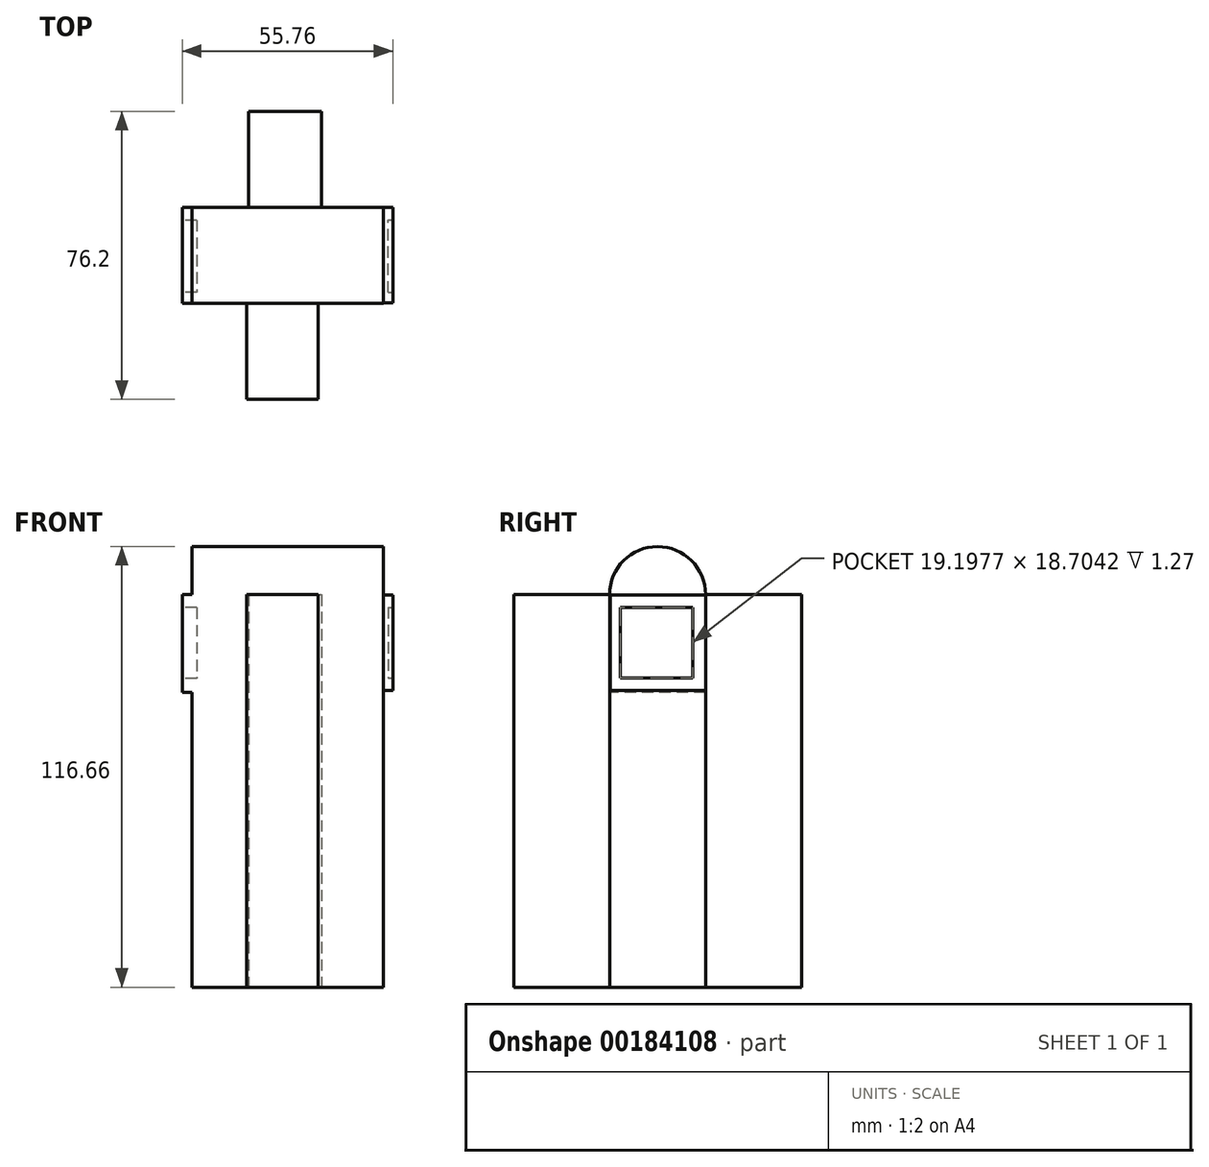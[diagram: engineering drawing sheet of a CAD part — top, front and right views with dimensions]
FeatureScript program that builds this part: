
annotation { "Feature Type Name" : "Feature", "Feature Type Description" : "" }
export const myFeature = defineFeature(function(context is Context, id is Id, definition is map)
    precondition{}
    {
        {
            var Q0;
            Q0=qCreatedBy(makeId("Front.planeOp"),FACE);
            var sketch = newSketch(context, id + "F0", { "sketchPlane" : qUnion([Q0])});
            skLineSegment(sketch, "E0.bottom", {"start": v(-23.52, 51.72) * mm, "end": v(27.16, 51.72) * mm});
            skLineSegment(sketch, "E0.top", {"start": v(-23.52, -52.24) * mm, "end": v(27.16, -52.24) * mm});
            skLineSegment(sketch, "E0.left", {"start": v(-23.52, 51.72) * mm, "end": v(-23.52, -52.24) * mm});
            skLineSegment(sketch, "E0.right", {"start": v(27.16, 51.72) * mm, "end": v(27.16, -52.24) * mm});
            skSolve(sketch);
        }
        {
            var Q0;
            Q0=makeQuery(id+"F0.imprint","IMPRINT",FACE,{"disambiguationData":[TD([[makeQuery(id+"F0.imprint","IMPRINT",EDGE,{"derivedFrom":sQuery(id+"F0.wireOp",EDGE,"E0.bottom")}),-1.0]])]});
            extrude(context, id + "F1", {"entities" : qUnion([Q0]), "depth" : 25.4 * mm});
        }
        {
            var Q0;
            Q0=makeQuery(id+"F1.opExtrude","SWEPT_FACE",FACE,{"disambiguationData":[OSD([sQuery(id+"F0.wireOp",EDGE,"E0.right")])]});
            var sketch = newSketch(context, id + "F2", { "sketchPlane" : qUnion([Q0])});
            skArc(sketch, "E1", {"start": v(0, 51.72) * mm, "mid": v(-12.7, 64.42) * mm, "end": v(-25.4, 51.72) * mm});
            skSolve(sketch);
        }
        {
            var Q0;
            Q0=makeQuery(id+"F1.opExtrude","SWEPT_FACE",FACE,{"disambiguationData":[OSD([sQuery(id+"F0.wireOp",EDGE,"E0.left")])]});
            var sketch = newSketch(context, id + "F3", { "sketchPlane" : qUnion([Q0])});
            skArc(sketch, "E2", {"start": v(25.4, 51.72) * mm, "mid": v(12.7, 64.42) * mm, "end": v(0, 51.72) * mm});
            skSolve(sketch);
        }
        {
            var Q0;
            Q0=makeQuery(id+"F1.opExtrude","CAP_FACE",FACE,{"disambiguationData":[OSD([sQuery(id+"F0.wireOp",EDGE,"E0.bottom"),sQuery(id+"F0.wireOp",EDGE,"E0.top"),sQuery(id+"F0.wireOp",EDGE,"E0.left"),sQuery(id+"F0.wireOp",EDGE,"E0.right")])],"isStart":false});
            var sketch = newSketch(context, id + "F4", { "sketchPlane" : qUnion([Q0])});
            skLineSegment(sketch, "E3", {"start": v(-8.94, 51.72) * mm, "end": v(-8.94, -52.24) * mm});
            skLineSegment(sketch, "E4", {"start": v(9.98, 51.72) * mm, "end": v(9.98, -52.24) * mm});
            skSolve(sketch);
        }
        {
            var Q0;
            {var subQ0=sQuery(id+"F4.wireOp",EDGE,"E3");Q0=makeQuery(id+"F4.imprint","IMPRINT",FACE,{"disambiguationData":[TD([[makeQuery(id+"F4.imprint","IMPRINT",EDGE,{"derivedFrom":subQ0}),1.0]])]});}
            extrude(context, id + "F5", {"entities" : qUnion([Q0]), "operationType" : NewBodyOperationType.ADD, "depth" : 25.4 * mm});
        }
        {
            var Q0;
            Q0=makeQuery(id+"F1.opExtrude","CAP_FACE",FACE,{"disambiguationData":[OSD([sQuery(id+"F0.wireOp",EDGE,"E0.bottom"),sQuery(id+"F0.wireOp",EDGE,"E0.top"),sQuery(id+"F0.wireOp",EDGE,"E0.left"),sQuery(id+"F0.wireOp",EDGE,"E0.right")])],"isStart":true});
            var sketch = newSketch(context, id + "F6", { "sketchPlane" : qUnion([Q0])});
            skLineSegment(sketch, "E5", {"start": v(8.5, 51.72) * mm, "end": v(8.5, -52.24) * mm});
            skLineSegment(sketch, "E6", {"start": v(-10.77, 51.72) * mm, "end": v(-10.77, -52.24) * mm});
            skPoint(sketch, "E7.end.orphan", {"position": v(8.5, -52.24) * mm});
            skSolve(sketch);
        }
        {
            var Q0;
            {var subQ0=sQuery(id+"F6.wireOp",EDGE,"E5");Q0=makeQuery(id+"F6.imprint","IMPRINT",FACE,{"disambiguationData":[TD([[makeQuery(id+"F6.imprint","IMPRINT",EDGE,{"derivedFrom":subQ0}),-1.0]])]});}
            extrude(context, id + "F7", {"entities" : qUnion([Q0]), "operationType" : NewBodyOperationType.ADD, "depth" : 25.4 * mm});
        }
        {
            var Q0;
            {var subQ0=sQuery(id+"F0.wireOp",EDGE,"E0.bottom");Q0=makeQuery(id+"F7.boolean.opBoolean","MERGE",FACE,{"derivedFrom":[makeQuery(id+"F5.boolean.opBoolean","MERGE",FACE,{"derivedFrom":[makeQuery(id+"F1.opExtrude","SWEPT_FACE",FACE,{"disambiguationData":[OSD([subQ0])]}),makeQuery(id+"F5.opExtrude","SWEPT_FACE",FACE,{"disambiguationData":[OSD([subQ0])]})]}),makeQuery(id+"F7.opExtrude","SWEPT_FACE",FACE,{"disambiguationData":[OSD([subQ0])]})]});}
            var sketch = newSketch(context, id + "F8", { "sketchPlane" : qUnion([Q0])});
            skLineSegment(sketch, "E8", {"start": v(-23.52, -12.7) * mm, "end": v(27.16, -12.7) * mm});
            skSolve(sketch);
        }
        {
            var Q0;
            Q0=makeQuery(id+"F3.imprint","IMPRINT",FACE,{"disambiguationData":[TD([[makeQuery(id+"F3.imprint","IMPRINT",EDGE,{"derivedFrom":sQuery(id+"F3.wireOp",EDGE,"E2")}),1.0]])]});
            var Q1;
            Q1=sQuery(id+"F8.wireOp",EDGE,"E8");
            sweep(context, id + "F9", {"operationType" : NewBodyOperationType.ADD, "profiles" : qUnion([Q0]), "path" : qUnion([Q1])});
        }
        {
            var Q0;
            {var subQ0=sQuery(id+"F0.wireOp",EDGE,"E0.right");Q0=makeQuery(id+"F2.imprint","IMPRINT",FACE,{"disambiguationData":[TD([[makeQuery(id+"F2.imprint","IMPRINT",EDGE,{"derivedFrom":makeQuery(id+"F1.opExtrude","CAP_EDGE",EDGE,{"disambiguationData":[OSD([subQ0])],"isStart":true})}),-1.0]])]});}
            var sketch = newSketch(context, id + "F10", { "sketchPlane" : qUnion([Q0])});
            skPoint(sketch, "E9", {"position": v(-25.25, 0) * mm});
            skPoint(sketch, "E10", {"position": v(-25.25, 26.38) * mm});
            skPoint(sketch, "E11", {"position": v(0, 26.38) * mm});
            skPoint(sketch, "E12", {"position": v(-25.25, 51.55) * mm});
            skPoint(sketch, "E13", {"position": v(0, 51.55) * mm});
            skLineSegment(sketch, "E14.bottom", {"start": v(-25.25, 51.55) * mm, "end": v(0, 51.55) * mm});
            skLineSegment(sketch, "E14.top", {"start": v(-25.25, 26.38) * mm, "end": v(0, 26.38) * mm});
            skLineSegment(sketch, "E14.left", {"start": v(-25.25, 51.55) * mm, "end": v(-25.25, 26.38) * mm});
            skLineSegment(sketch, "E14.right", {"start": v(0, 51.55) * mm, "end": v(0, 26.38) * mm});
            skSolve(sketch);
        }
        {
            var Q0;
            Q0=makeQuery(id+"F10.imprint","IMPRINT",FACE,{"disambiguationData":[TD([[makeQuery(id+"F10.imprint","IMPRINT",EDGE,{"derivedFrom":sQuery(id+"F10.wireOp",EDGE,"E14.bottom")}),-1.0]])]});
            extrude(context, id + "F11", {"entities" : qUnion([Q0]), "operationType" : NewBodyOperationType.ADD, "depth" : 2.54 * mm});
        }
        {
            var Q0;
            {var subQ0=sQuery(id+"F0.wireOp",EDGE,"E0.right");Q0=makeQuery(id+"F2.imprint","IMPRINT",FACE,{"disambiguationData":[TD([[makeQuery(id+"F2.imprint","IMPRINT",EDGE,{"derivedFrom":makeQuery(id+"F1.opExtrude","CAP_EDGE",EDGE,{"disambiguationData":[OSD([subQ0])],"isStart":true})}),-1.0]])]});}
            var sketch = newSketch(context, id + "F12", { "sketchPlane" : qUnion([Q0])});
            skLineSegment(sketch, "E15", {"start": v(-25.25, 26.2) * mm, "end": v(-25.25, -52.07) * mm});
            skLineSegment(sketch, "E16", {"start": v(-25.25, -52.07) * mm, "end": v(0, 25.69) * mm});
            skSolve(sketch);
        }
        {
            var Q0;
            {var subQ0=sQuery(id+"F0.wireOp",EDGE,"E0.right");Q0=makeQuery(id+"F2.imprint","IMPRINT",FACE,{"disambiguationData":[TD([[makeQuery(id+"F2.imprint","IMPRINT",EDGE,{"derivedFrom":makeQuery(id+"F1.opExtrude","CAP_EDGE",EDGE,{"disambiguationData":[OSD([subQ0])],"isStart":true})}),-1.0]])]});}
            var sketch = newSketch(context, id + "F13", { "sketchPlane" : qUnion([Q0])});
            skLineSegment(sketch, "E17", {"start": v(-23.7, 26.2) * mm, "end": v(-23.7, -45.82) * mm});
            skLineSegment(sketch, "E18", {"start": v(-23.7, -45.82) * mm, "end": v(-23.7, 26.2) * mm});
            skLineSegment(sketch, "E19", {"start": v(-20.4, 25.86) * mm, "end": v(-20.4, -36.27) * mm});
            skLineSegment(sketch, "E20", {"start": v(-16.57, 25.86) * mm, "end": v(-16.57, -24.65) * mm});
            skLineSegment(sketch, "E21", {"start": v(-12.93, 25.86) * mm, "end": v(-12.93, -13.02) * mm});
            skLineSegment(sketch, "E22", {"start": v(-9.29, 25.86) * mm, "end": v(-9.29, -1.9) * mm});
            skLineSegment(sketch, "E23", {"start": v(-5.81, 25.69) * mm, "end": v(-5.81, 8.5) * mm});
            skLineSegment(sketch, "E24", {"start": v(-2.52, 25.86) * mm, "end": v(-2.52, 18.57) * mm});
            skLineSegment(sketch, "E25", {"start": v(-2.52, 18.57) * mm, "end": v(-23.7, 18.57) * mm});
            skLineSegment(sketch, "E26", {"start": v(-23.7, 18.57) * mm, "end": v(-5.81, 8.5) * mm});
            skLineSegment(sketch, "E27", {"start": v(-5.81, 8.5) * mm, "end": v(-23.7, 8.5) * mm});
            skLineSegment(sketch, "E28", {"start": v(-23.7, 8.5) * mm, "end": v(-9.29, -1.9) * mm});
            skLineSegment(sketch, "E29", {"start": v(-9.29, -1.9) * mm, "end": v(-23.7, -1.9) * mm});
            skLineSegment(sketch, "E30", {"start": v(-23.7, -1.9) * mm, "end": v(-12.93, -13.02) * mm});
            skLineSegment(sketch, "E31", {"start": v(-12.93, -13.02) * mm, "end": v(-23.7, -13.02) * mm});
            skLineSegment(sketch, "E32", {"start": v(-23.7, -13.02) * mm, "end": v(-16.57, -24.65) * mm});
            skLineSegment(sketch, "E33", {"start": v(-16.57, -24.65) * mm, "end": v(-23.7, -24.65) * mm});
            skLineSegment(sketch, "E34", {"start": v(-23.7, -24.65) * mm, "end": v(-20.4, -36.27) * mm});
            skLineSegment(sketch, "E35", {"start": v(-23.7, -36.27) * mm, "end": v(-22.05, -41.3) * mm});
            skLineSegment(sketch, "E36", {"start": v(-22.05, -41.3) * mm, "end": v(-23.7, -41.3) * mm});
            skLineSegment(sketch, "E37", {"start": v(-23.7, -41.3) * mm, "end": v(-23.7, -45.82) * mm});
            skSolve(sketch);
        }
        {
            var Q0;
            {var subQ0=sQuery(id+"F0.wireOp",EDGE,"E0.right");Q0=makeQuery(id+"F2.imprint","IMPRINT",FACE,{"disambiguationData":[TD([[makeQuery(id+"F2.imprint","IMPRINT",EDGE,{"derivedFrom":makeQuery(id+"F1.opExtrude","CAP_EDGE",EDGE,{"disambiguationData":[OSD([subQ0])],"isStart":true})}),-1.0]])]});}
            var sketch = newSketch(context, id + "F14", { "sketchPlane" : qUnion([Q0])});
            skSolve(sketch);
        }
        {
            var Q0;
            Q0=sQuery(id+"F13.wireOp",EDGE,"E25");
            extrude(context, id + "F15", {"bodyType" : ToolBodyType.SURFACE, "surfaceEntities" : qUnion([Q0]), "depth" : 1.27 * mm});
        }
        {
            var Q0;
            Q0=sQuery(id+"F13.wireOp",EDGE,"E18");
            extrude(context, id + "F16", {"bodyType" : ToolBodyType.SURFACE, "operationType" : NewBodyOperationType.ADD, "surfaceEntities" : qUnion([Q0]), "depth" : 1.27 * mm});
        }
        {
            var Q0;
            Q0=sQuery(id+"F13.wireOp",EDGE,"E19");
            extrude(context, id + "F17", {"bodyType" : ToolBodyType.SURFACE, "surfaceEntities" : qUnion([Q0]), "depth" : 1.27 * mm});
        }
        {
            var Q0;
            Q0=sQuery(id+"F13.wireOp",EDGE,"E20");
            extrude(context, id + "F18", {"bodyType" : ToolBodyType.SURFACE, "surfaceEntities" : qUnion([Q0]), "depth" : 1.27 * mm});
        }
        {
            var Q0;
            Q0=sQuery(id+"F13.wireOp",EDGE,"E21");
            var Q1;
            Q1=sQuery(id+"F13.wireOp",EDGE,"E22");
            extrude(context, id + "F19", {"bodyType" : ToolBodyType.SURFACE, "surfaceEntities" : qUnion([Q0, Q1]), "depth" : 1.27 * mm});
        }
        {
            var Q0;
            Q0=sQuery(id+"F13.wireOp",EDGE,"E23");
            var Q1;
            Q1=sQuery(id+"F13.wireOp",EDGE,"E24");
            extrude(context, id + "F20", {"bodyType" : ToolBodyType.SURFACE, "surfaceEntities" : qUnion([Q0, Q1]), "depth" : 1.27 * mm});
        }
        {
            var Q0;
            Q0=sQuery(id+"F13.wireOp",EDGE,"E26");
            extrude(context, id + "F21", {"bodyType" : ToolBodyType.SURFACE, "surfaceEntities" : qUnion([Q0]), "depth" : 1.27 * mm});
        }
        {
            var Q0;
            Q0=sQuery(id+"F13.wireOp",EDGE,"E27");
            extrude(context, id + "F22", {"bodyType" : ToolBodyType.SURFACE, "surfaceEntities" : qUnion([Q0]), "depth" : 1.27 * mm});
        }
        {
            var Q0;
            Q0=sQuery(id+"F13.wireOp",EDGE,"E28");
            extrude(context, id + "F23", {"bodyType" : ToolBodyType.SURFACE, "surfaceEntities" : qUnion([Q0]), "depth" : 1.27 * mm});
        }
        {
            var Q0;
            Q0=sQuery(id+"F13.wireOp",EDGE,"E29");
            extrude(context, id + "F24", {"bodyType" : ToolBodyType.SURFACE, "surfaceEntities" : qUnion([Q0]), "depth" : 1.27 * mm});
        }
        {
            var Q0;
            Q0=sQuery(id+"F13.wireOp",EDGE,"E30");
            var Q1;
            Q1=sQuery(id+"F13.wireOp",EDGE,"E31");
            extrude(context, id + "F25", {"bodyType" : ToolBodyType.SURFACE, "surfaceEntities" : qUnion([Q0, Q1]), "depth" : 1.27 * mm});
        }
        {
            var Q0;
            Q0=sQuery(id+"F13.wireOp",EDGE,"E32");
            var Q1;
            Q1=sQuery(id+"F13.wireOp",EDGE,"E33");
            extrude(context, id + "F26", {"bodyType" : ToolBodyType.SURFACE, "surfaceEntities" : qUnion([Q0, Q1]), "depth" : 1.27 * mm});
        }
        {
            var Q0;
            Q0=sQuery(id+"F13.wireOp",EDGE,"E34");
            var Q1;
            Q1=sQuery(id+"F13.wireOp",EDGE,"E35");
            extrude(context, id + "F27", {"bodyType" : ToolBodyType.SURFACE, "surfaceEntities" : qUnion([Q0, Q1]), "depth" : 1.27 * mm});
        }
        {
            var Q0;
            Q0=makeQuery(id+"F11.opExtrude","CAP_FACE",FACE,{"disambiguationData":[OSD([sQuery(id+"F10.wireOp",EDGE,"E14.bottom"),sQuery(id+"F10.wireOp",EDGE,"E14.top"),sQuery(id+"F10.wireOp",EDGE,"E14.left"),sQuery(id+"F10.wireOp",EDGE,"E14.right")])],"isStart":false});
            var sketch = newSketch(context, id + "F28", { "sketchPlane" : qUnion([Q0])});
            skLineSegment(sketch, "E38.bottom", {"start": v(-22.53, 48.32) * mm, "end": v(-3.33, 48.32) * mm});
            skLineSegment(sketch, "E38.top", {"start": v(-22.53, 29.62) * mm, "end": v(-3.33, 29.62) * mm});
            skLineSegment(sketch, "E38.left", {"start": v(-22.53, 48.32) * mm, "end": v(-22.53, 29.62) * mm});
            skLineSegment(sketch, "E38.right", {"start": v(-3.33, 48.32) * mm, "end": v(-3.33, 29.62) * mm});
            skSolve(sketch);
        }
        {
            var Q0;
            Q0=makeQuery(id+"F28.imprint","IMPRINT",FACE,{"disambiguationData":[TD([[makeQuery(id+"F28.imprint","IMPRINT",EDGE,{"derivedFrom":sQuery(id+"F28.wireOp",EDGE,"E38.bottom")}),-1.0]])]});
            extrude(context, id + "F29", {"entities" : qUnion([Q0]), "operationType" : NewBodyOperationType.REMOVE, "oppositeDirection" : true, "depth" : 1.27 * mm});
        }
        {
            var Q0;
            {var subQ0=sQuery(id+"F0.wireOp",EDGE,"E0.left");Q0=makeQuery(id+"F9.boolean.opBoolean","MERGE",FACE,{"derivedFrom":[makeQuery(id+"F1.opExtrude","SWEPT_FACE",FACE,{"disambiguationData":[OSD([subQ0])]}),makeQuery(id+"F9.opSweep","CAP_FACE",FACE,{"disambiguationData":[OSD([sQuery(id+"F0.wireOp",EDGE,"E0.bottom"),subQ0,sQuery(id+"F3.wireOp",EDGE,"E2"),sQuery(id+"F8.wireOp",VERTEX,"E8.start")])],"isStart":true})]});}
            var sketch = newSketch(context, id + "F30", { "sketchPlane" : qUnion([Q0])});
            skLineSegment(sketch, "E39.bottom", {"start": v(3.38, 48.25) * mm, "end": v(22.48, 48.25) * mm});
            skLineSegment(sketch, "E39.top", {"start": v(3.38, 29.5) * mm, "end": v(22.48, 29.5) * mm});
            skLineSegment(sketch, "E39.left", {"start": v(3.38, 48.25) * mm, "end": v(3.38, 29.5) * mm});
            skLineSegment(sketch, "E39.right", {"start": v(22.48, 48.25) * mm, "end": v(22.48, 29.5) * mm});
            skSolve(sketch);
        }
        {
            var Q0;
            Q0=makeQuery(id+"F30.imprint","IMPRINT",FACE,{"disambiguationData":[TD([[makeQuery(id+"F30.imprint","IMPRINT",EDGE,{"derivedFrom":sQuery(id+"F30.wireOp",EDGE,"E39.bottom")}),-1.0]])]});
            extrude(context, id + "F31", {"entities" : qUnion([Q0]), "operationType" : NewBodyOperationType.REMOVE, "oppositeDirection" : true, "depth" : 1.27 * mm});
        }
        {
            var Q0;
            {var subQ0=sQuery(id+"F0.wireOp",EDGE,"E0.left");Q0=makeQuery(id+"F9.boolean.opBoolean","MERGE",FACE,{"derivedFrom":[makeQuery(id+"F1.opExtrude","SWEPT_FACE",FACE,{"disambiguationData":[OSD([subQ0])]}),makeQuery(id+"F9.opSweep","CAP_FACE",FACE,{"disambiguationData":[OSD([sQuery(id+"F0.wireOp",EDGE,"E0.bottom"),subQ0,sQuery(id+"F3.wireOp",EDGE,"E2"),sQuery(id+"F8.wireOp",VERTEX,"E8.start")])],"isStart":true})]});}
            var sketch = newSketch(context, id + "F32", { "sketchPlane" : qUnion([Q0])});
            skLineSegment(sketch, "E40.bottom", {"start": v(0, 51.72) * mm, "end": v(25.4, 51.72) * mm});
            skLineSegment(sketch, "E40.top", {"start": v(0, 25.86) * mm, "end": v(25.4, 25.86) * mm});
            skLineSegment(sketch, "E40.left", {"start": v(0, 51.72) * mm, "end": v(0, 25.86) * mm});
            skLineSegment(sketch, "E40.right", {"start": v(25.4, 51.72) * mm, "end": v(25.4, 25.86) * mm});
            skSolve(sketch);
        }
        {
            var Q0;
            Q0=makeQuery(id+"F32.imprint","IMPRINT",FACE,{"disambiguationData":[TD([[makeQuery(id+"F32.imprint","IMPRINT",EDGE,{"derivedFrom":sQuery(id+"F32.wireOp",EDGE,"E40.bottom")}),-1.0]])]});
            extrude(context, id + "F33", {"entities" : qUnion([Q0]), "operationType" : NewBodyOperationType.ADD, "depth" : 2.54 * mm});
        }
        {
            var Q0;
            {var subQ0=sQuery(id+"F0.wireOp",EDGE,"E0.top");var subQ2=sQuery(id+"F0.wireOp",EDGE,"E0.left");var subQ3=sQuery(id+"F0.wireOp",EDGE,"E0.bottom");Q0=makeQuery(id+"F33.boolean.opBoolean","SPLIT",FACE,{"disambiguationData":[TD([makeQuery(id+"F1.opExtrude","SWEPT_FACE",FACE,{"disambiguationData":[OSD([subQ0])]})])],"derivedFrom":makeQuery(id+"F9.boolean.opBoolean","MERGE",FACE,{"derivedFrom":[makeQuery(id+"F1.opExtrude","SWEPT_FACE",FACE,{"disambiguationData":[OSD([subQ2])]}),makeQuery(id+"F9.opSweep","CAP_FACE",FACE,{"disambiguationData":[OSD([subQ3,subQ2,sQuery(id+"F3.wireOp",EDGE,"E2"),sQuery(id+"F8.wireOp",VERTEX,"E8.start")])],"isStart":true})]})});}
            var sketch = newSketch(context, id + "F34", { "sketchPlane" : qUnion([Q0])});
            skLineSegment(sketch, "E41", {"start": v(25.4, 25.86) * mm, "end": v(0, -52.24) * mm});
            skSolve(sketch);
        }
        {
            var Q0;
            Q0=makeQuery(id+"F34.imprint","IMPRINT",FACE,{"disambiguationData":[TD([[makeQuery(id+"F34.imprint","IMPRINT",EDGE,{"derivedFrom":sQuery(id+"F34.wireOp",EDGE,"E41")}),-1.0]])]});
            var sketch = newSketch(context, id + "F35", { "sketchPlane" : qUnion([Q0])});
            skLineSegment(sketch, "E42", {"start": v(2.52, 25.69) * mm, "end": v(2.52, -43.04) * mm});
            skLineSegment(sketch, "E43", {"start": v(2.52, -43.04) * mm, "end": v(2.52, 25.69) * mm});
            skLineSegment(sketch, "E44", {"start": v(5.64, 25.69) * mm, "end": v(5.64, -34.71) * mm});
            skLineSegment(sketch, "E45", {"start": v(9.29, 25.69) * mm, "end": v(9.29, -23.26) * mm});
            skLineSegment(sketch, "E46", {"start": v(13.1, 25.69) * mm, "end": v(13.1, -13.02) * mm});
            skLineSegment(sketch, "E47", {"start": v(16.75, 25.69) * mm, "end": v(16.75, 0) * mm});
            skLineSegment(sketch, "E48", {"start": v(20.4, 25.69) * mm, "end": v(20.4, 11.63) * mm});
            skLineSegment(sketch, "E49", {"start": v(23.86, 25.69) * mm, "end": v(23.86, 20.83) * mm});
            skLineSegment(sketch, "E50", {"start": v(25.43, 25.69) * mm, "end": v(0, -52.07) * mm});
            skLineSegment(sketch, "E51", {"start": v(2.52, 18.57) * mm, "end": v(23.1, 18.57) * mm});
            skLineSegment(sketch, "E52", {"start": v(2.52, 8.16) * mm, "end": v(20.4, 8.16) * mm});
            skLineSegment(sketch, "E53", {"start": v(2.52, -1.74) * mm, "end": v(16.46, -1.74) * mm});
            skLineSegment(sketch, "E54", {"start": v(2.52, -13.36) * mm, "end": v(12.66, -13.36) * mm});
            skLineSegment(sketch, "E55", {"start": v(2.52, -23.26) * mm, "end": v(9.29, -23.26) * mm});
            skLineSegment(sketch, "E56", {"start": v(9.29, -23.26) * mm, "end": v(2.52, -34.71) * mm});
            skLineSegment(sketch, "E57", {"start": v(5.64, -34.71) * mm, "end": v(2.52, -34.71) * mm});
            skLineSegment(sketch, "E58", {"start": v(12.66, -13.36) * mm, "end": v(2.52, -23.26) * mm});
            skLineSegment(sketch, "E59", {"start": v(16.46, -1.74) * mm, "end": v(2.52, -13.36) * mm});
            skLineSegment(sketch, "E60", {"start": v(20.4, 8.16) * mm, "end": v(2.52, -1.74) * mm});
            skLineSegment(sketch, "E61", {"start": v(23.1, 18.57) * mm, "end": v(2.52, 8.16) * mm});
            skSolve(sketch);
        }
        {
            var Q0;
            Q0=sQuery(id+"F12.wireOp",EDGE,"E16");
            extrude(context, id + "F36", {"bodyType" : ToolBodyType.SURFACE, "surfaceEntities" : qUnion([Q0]), "depth" : 1.27 * mm});
        }
        {
            var Q0;
            Q0=sQuery(id+"F35.wireOp",EDGE,"E42");
            var Q1;
            Q1=sQuery(id+"F35.wireOp",EDGE,"E44");
            var Q2;
            Q2=sQuery(id+"F35.wireOp",EDGE,"E45");
            var Q3;
            Q3=sQuery(id+"F35.wireOp",EDGE,"E46");
            var Q4;
            Q4=sQuery(id+"F35.wireOp",EDGE,"E47");
            extrude(context, id + "F37", {"bodyType" : ToolBodyType.SURFACE, "surfaceEntities" : qUnion([Q0, Q1, Q2, Q3, Q4]), "depth" : 1.27 * mm});
        }
        {
            var Q0;
            Q0=sQuery(id+"F34.wireOp",EDGE,"E41");
            extrude(context, id + "F38", {"bodyType" : ToolBodyType.SURFACE, "surfaceEntities" : qUnion([Q0]), "depth" : 1.27 * mm});
        }
        {
            var Q0;
            {var subQ0=sQuery(id+"F0.wireOp",EDGE,"E0.top");var subQ2=sQuery(id+"F0.wireOp",EDGE,"E0.left");var subQ3=sQuery(id+"F0.wireOp",EDGE,"E0.bottom");Q0=makeQuery(id+"F33.boolean.opBoolean","SPLIT",FACE,{"disambiguationData":[TD([makeQuery(id+"F1.opExtrude","SWEPT_FACE",FACE,{"disambiguationData":[OSD([subQ0])]})])],"derivedFrom":makeQuery(id+"F9.boolean.opBoolean","MERGE",FACE,{"derivedFrom":[makeQuery(id+"F1.opExtrude","SWEPT_FACE",FACE,{"disambiguationData":[OSD([subQ2])]}),makeQuery(id+"F9.opSweep","CAP_FACE",FACE,{"disambiguationData":[OSD([subQ3,subQ2,sQuery(id+"F3.wireOp",EDGE,"E2"),sQuery(id+"F8.wireOp",VERTEX,"E8.start")])],"isStart":true})]})});}
            var sketch = newSketch(context, id + "F39", { "sketchPlane" : qUnion([Q0])});
            skLineSegment(sketch, "E62", {"start": v(2.6, 18.22) * mm, "end": v(23.08, 18.22) * mm});
            skLineSegment(sketch, "E63", {"start": v(23.08, 18.22) * mm, "end": v(2.95, 8.33) * mm});
            skLineSegment(sketch, "E64", {"start": v(2.95, 8.33) * mm, "end": v(19.44, 8.33) * mm});
            skLineSegment(sketch, "E65", {"start": v(19.44, 8.33) * mm, "end": v(2.95, -2.95) * mm});
            skLineSegment(sketch, "E66", {"start": v(2.95, -2.95) * mm, "end": v(16.14, -2.95) * mm});
            skLineSegment(sketch, "E67", {"start": v(16.14, -2.95) * mm, "end": v(2.95, -13.88) * mm});
            skLineSegment(sketch, "E68", {"start": v(2.95, -13.88) * mm, "end": v(12.84, -13.88) * mm});
            skLineSegment(sketch, "E69", {"start": v(12.84, -13.88) * mm, "end": v(2.95, -25.34) * mm});
            skLineSegment(sketch, "E70", {"start": v(2.95, -25.34) * mm, "end": v(9.2, -25.34) * mm});
            skLineSegment(sketch, "E71", {"start": v(9.2, -25.34) * mm, "end": v(2.95, -36.27) * mm});
            skLineSegment(sketch, "E72", {"start": v(2.95, -36.27) * mm, "end": v(5.04, -37.47) * mm});
            skSolve(sketch);
        }
        {
            var Q0;
            Q0=sQuery(id+"F13.wireOp",EDGE,"E25");
            extrude(context, id + "F40", {"bodyType" : ToolBodyType.SURFACE, "surfaceEntities" : qUnion([Q0]), "depth" : 1.27 * mm});
        }
        {
            var Q0;
            Q0=sQuery(id+"F39.wireOp",EDGE,"E62");
            extrude(context, id + "F41", {"bodyType" : ToolBodyType.SURFACE, "surfaceEntities" : qUnion([Q0]), "depth" : 1.27 * mm});
        }
        {
            var Q0;
            {var subQ0=sQuery(id+"F0.wireOp",EDGE,"E0.top");var subQ2=sQuery(id+"F0.wireOp",EDGE,"E0.left");var subQ3=sQuery(id+"F0.wireOp",EDGE,"E0.bottom");Q0=makeQuery(id+"F33.boolean.opBoolean","SPLIT",FACE,{"disambiguationData":[TD([makeQuery(id+"F1.opExtrude","SWEPT_FACE",FACE,{"disambiguationData":[OSD([subQ0])]})])],"derivedFrom":makeQuery(id+"F9.boolean.opBoolean","MERGE",FACE,{"derivedFrom":[makeQuery(id+"F1.opExtrude","SWEPT_FACE",FACE,{"disambiguationData":[OSD([subQ2])]}),makeQuery(id+"F9.opSweep","CAP_FACE",FACE,{"disambiguationData":[OSD([subQ3,subQ2,sQuery(id+"F3.wireOp",EDGE,"E2"),sQuery(id+"F8.wireOp",VERTEX,"E8.start")])],"isStart":true})]})});}
            var sketch = newSketch(context, id + "F42", { "sketchPlane" : qUnion([Q0])});
            skLineSegment(sketch, "E73", {"start": v(23.43, 18.05) * mm, "end": v(2.78, 7.64) * mm});
            skSolve(sketch);
        }
        {
            var Q0;
            Q0=sQuery(id+"F42.wireOp",EDGE,"E73");
            extrude(context, id + "F43", {"bodyType" : ToolBodyType.SURFACE, "surfaceEntities" : qUnion([Q0]), "depth" : 1.27 * mm});
        }
        {
            var Q0;
            {var subQ0=sQuery(id+"F0.wireOp",EDGE,"E0.top");var subQ2=sQuery(id+"F0.wireOp",EDGE,"E0.left");var subQ3=sQuery(id+"F0.wireOp",EDGE,"E0.bottom");Q0=makeQuery(id+"F33.boolean.opBoolean","SPLIT",FACE,{"disambiguationData":[TD([makeQuery(id+"F1.opExtrude","SWEPT_FACE",FACE,{"disambiguationData":[OSD([subQ0])]})])],"derivedFrom":makeQuery(id+"F9.boolean.opBoolean","MERGE",FACE,{"derivedFrom":[makeQuery(id+"F1.opExtrude","SWEPT_FACE",FACE,{"disambiguationData":[OSD([subQ2])]}),makeQuery(id+"F9.opSweep","CAP_FACE",FACE,{"disambiguationData":[OSD([subQ3,subQ2,sQuery(id+"F3.wireOp",EDGE,"E2"),sQuery(id+"F8.wireOp",VERTEX,"E8.start")])],"isStart":true})]})});}
            var sketch = newSketch(context, id + "F44", { "sketchPlane" : qUnion([Q0])});
            skLineSegment(sketch, "E74", {"start": v(2.43, 7.12) * mm, "end": v(18.74, 7.12) * mm});
            skSolve(sketch);
        }
        {
            var Q0;
            {var subQ0=sQuery(id+"F0.wireOp",EDGE,"E0.left");Q0=makeQuery(id+"F44.imprint","IMPRINT",FACE,{"disambiguationData":[TD([[makeQuery(id+"F44.imprint","IMPRINT",EDGE,{"derivedFrom":makeQuery(id+"F1.opExtrude","CAP_EDGE",EDGE,{"disambiguationData":[OSD([subQ0])],"isStart":true})}),1.0]])]});}
            var sketch = newSketch(context, id + "F45", { "sketchPlane" : qUnion([Q0])});
            skSolve(sketch);
        }
        {
            var Q0;
            Q0=sQuery(id+"F44.wireOp",EDGE,"E74");
            extrude(context, id + "F46", {"bodyType" : ToolBodyType.SURFACE, "surfaceEntities" : qUnion([Q0]), "depth" : 1.27 * mm});
        }
        {
            var Q0;
            {var subQ0=sQuery(id+"F0.wireOp",EDGE,"E0.left");Q0=makeQuery(id+"F45.imprint","IMPRINT",FACE,{"disambiguationData":[TD([[makeQuery(id+"F45.imprint","IMPRINT",EDGE,{"derivedFrom":makeQuery(id+"F44.imprint","IMPRINT",EDGE,{"derivedFrom":makeQuery(id+"F1.opExtrude","CAP_EDGE",EDGE,{"disambiguationData":[OSD([subQ0])],"isStart":true})})}),1.0]])]});}
            var sketch = newSketch(context, id + "F47", { "sketchPlane" : qUnion([Q0])});
            skLineSegment(sketch, "E75", {"start": v(19.6, 7.07) * mm, "end": v(3.12, -2.78) * mm});
            skSolve(sketch);
        }
        {
            var Q0;
            Q0=sQuery(id+"F47.wireOp",EDGE,"E75");
            extrude(context, id + "F48", {"bodyType" : ToolBodyType.SURFACE, "surfaceEntities" : qUnion([Q0]), "depth" : 1.27 * mm});
        }
        {
            var Q0;
            {var subQ0=sQuery(id+"F0.wireOp",EDGE,"E0.left");Q0=makeQuery(id+"F45.imprint","IMPRINT",FACE,{"disambiguationData":[TD([[makeQuery(id+"F45.imprint","IMPRINT",EDGE,{"derivedFrom":makeQuery(id+"F44.imprint","IMPRINT",EDGE,{"derivedFrom":makeQuery(id+"F1.opExtrude","CAP_EDGE",EDGE,{"disambiguationData":[OSD([subQ0])],"isStart":true})})}),1.0]])]});}
            var sketch = newSketch(context, id + "F49", { "sketchPlane" : qUnion([Q0])});
            skLineSegment(sketch, "E76", {"start": v(2.78, -3.3) * mm, "end": v(15.8, -3.3) * mm});
            skLineSegment(sketch, "E77", {"start": v(15.8, -3.3) * mm, "end": v(2.78, -12.67) * mm});
            skLineSegment(sketch, "E78", {"start": v(2.78, -12.67) * mm, "end": v(13.02, -12.67) * mm});
            skLineSegment(sketch, "E79", {"start": v(13.02, -12.67) * mm, "end": v(2.78, -24.12) * mm});
            skLineSegment(sketch, "E80", {"start": v(2.78, -24.12) * mm, "end": v(9.2, -24.12) * mm});
            skLineSegment(sketch, "E81", {"start": v(9.2, -24.12) * mm, "end": v(2.78, -31.3) * mm});
            skLineSegment(sketch, "E82", {"start": v(2.78, -31.3) * mm, "end": v(6.77, -31.3) * mm});
            skLineSegment(sketch, "E83", {"start": v(6.77, -31.3) * mm, "end": v(2.78, -37.66) * mm});
            skSolve(sketch);
        }
        {
            var Q0;
            Q0=sQuery(id+"F49.wireOp",EDGE,"E76");
            var Q1;
            Q1=sQuery(id+"F49.wireOp",EDGE,"E77");
            var Q2;
            Q2=sQuery(id+"F49.wireOp",EDGE,"E78");
            var Q3;
            Q3=sQuery(id+"F49.wireOp",EDGE,"E79");
            var Q4;
            Q4=sQuery(id+"F49.wireOp",EDGE,"E80");
            var Q5;
            Q5=sQuery(id+"F49.wireOp",EDGE,"E81");
            extrude(context, id + "F50", {"bodyType" : ToolBodyType.SURFACE, "surfaceEntities" : qUnion([Q0, Q1, Q2, Q3, Q4, Q5]), "depth" : 1.27 * mm});
        }
        {
            var Q0;
            {var subQ0=sQuery(id+"F0.wireOp",EDGE,"E0.left");Q0=makeQuery(id+"F45.imprint","IMPRINT",FACE,{"disambiguationData":[TD([[makeQuery(id+"F45.imprint","IMPRINT",EDGE,{"derivedFrom":makeQuery(id+"F44.imprint","IMPRINT",EDGE,{"derivedFrom":makeQuery(id+"F1.opExtrude","CAP_EDGE",EDGE,{"disambiguationData":[OSD([subQ0])],"isStart":true})})}),1.0]])]});}
            var sketch = newSketch(context, id + "F51", { "sketchPlane" : qUnion([Q0])});
            skLineSegment(sketch, "E84", {"start": v(2.86, -30.92) * mm, "end": v(7.39, -30.92) * mm});
            skLineSegment(sketch, "E85", {"start": v(7.39, -30.92) * mm, "end": v(2.7, -37.2) * mm});
            skSolve(sketch);
        }
        {
            var Q0;
            Q0=sQuery(id+"F51.wireOp",EDGE,"E85");
            var Q1;
            Q1=sQuery(id+"F51.wireOp",EDGE,"E84");
            extrude(context, id + "F52", {"bodyType" : ToolBodyType.SURFACE, "surfaceEntities" : qUnion([Q0, Q1]), "depth" : 1.27 * mm});
        }
        {
            var Q0;
            Q0=makeQuery(id+"F5.opExtrude","CAP_FACE",FACE,{"disambiguationData":[OSD([sQuery(id+"F0.wireOp",EDGE,"E0.bottom"),sQuery(id+"F0.wireOp",EDGE,"E0.top"),sQuery(id+"F4.wireOp",EDGE,"E3"),sQuery(id+"F4.wireOp",EDGE,"E4")])],"isStart":false});
            var sketch = newSketch(context, id + "F53", { "sketchPlane" : qUnion([Q0])});
            skLineSegment(sketch, "E86", {"start": v(-5.71, 51.72) * mm, "end": v(-5.71, -53.54) * mm});
            skLineSegment(sketch, "E87", {"start": v(0, 51.72) * mm, "end": v(0, -52.24) * mm});
            skLineSegment(sketch, "E88", {"start": v(5.34, 51.72) * mm, "end": v(5.34, -52.24) * mm});
            skSolve(sketch);
        }
        {
            var Q0;
            {var subQ5=sQuery(id+"F53.wireOp",EDGE,"E87");Q0=makeQuery(id+"F53.imprint","IMPRINT",FACE,{"disambiguationData":[TD([[makeQuery(id+"F53.imprint","IMPRINT",EDGE,{"derivedFrom":subQ5}),-1.0]])]});}
            var sketch = newSketch(context, id + "F54", { "sketchPlane" : qUnion([Q0])});
            skLineSegment(sketch, "E89", {"start": v(-8.58, 38.15) * mm, "end": v(9.27, 38.15) * mm});
            skLineSegment(sketch, "E90", {"start": v(-8.82, 27.67) * mm, "end": v(9.27, 27.67) * mm});
            skLineSegment(sketch, "E91", {"start": v(-8.9, 17.55) * mm, "end": v(9.27, 17.55) * mm});
            skLineSegment(sketch, "E92", {"start": v(-8.68, 8.15) * mm, "end": v(9.27, 8.15) * mm});
            skLineSegment(sketch, "E93", {"start": v(-8.6, -3.78) * mm, "end": v(9.27, -3.78) * mm});
            skLineSegment(sketch, "E94", {"start": v(-8.79, -14.98) * mm, "end": v(9.27, -14.98) * mm});
            skLineSegment(sketch, "E95", {"start": v(-8.78, -26.19) * mm, "end": v(9.27, -26.19) * mm});
            skLineSegment(sketch, "E96", {"start": v(-8.63, -36.85) * mm, "end": v(9.27, -36.85) * mm});
            skSolve(sketch);
        }
        {
            var Q0;
            Q0=sQuery(id+"F53.wireOp",EDGE,"E88");
            var Q1;
            Q1=sQuery(id+"F53.wireOp",EDGE,"E87");
            var Q2;
            Q2=sQuery(id+"F53.wireOp",EDGE,"E86");
            extrude(context, id + "F55", {"bodyType" : ToolBodyType.SURFACE, "surfaceEntities" : qUnion([Q0, Q1, Q2]), "oppositeDirection" : true, "depth" : 1.27 * mm});
        }
        {
            var Q0;
            Q0=sQuery(id+"F54.wireOp",EDGE,"E89");
            var Q1;
            Q1=sQuery(id+"F54.wireOp",EDGE,"E90");
            var Q2;
            Q2=sQuery(id+"F54.wireOp",EDGE,"E91");
            var Q3;
            Q3=sQuery(id+"F54.wireOp",EDGE,"E92");
            var Q4;
            Q4=sQuery(id+"F54.wireOp",EDGE,"E93");
            var Q5;
            Q5=sQuery(id+"F54.wireOp",EDGE,"E94");
            var Q6;
            Q6=sQuery(id+"F54.wireOp",EDGE,"E95");
            var Q7;
            Q7=sQuery(id+"F54.wireOp",EDGE,"E96");
            extrude(context, id + "F56", {"bodyType" : ToolBodyType.SURFACE, "surfaceEntities" : qUnion([Q0, Q1, Q2, Q3, Q4, Q5, Q6, Q7]), "oppositeDirection" : true, "depth" : 1.27 * mm});
        }
        {
            var Q0;
            Q0=makeQuery(id+"F7.opExtrude","CAP_FACE",FACE,{"disambiguationData":[OSD([sQuery(id+"F0.wireOp",EDGE,"E0.bottom"),sQuery(id+"F0.wireOp",EDGE,"E0.top"),sQuery(id+"F6.wireOp",EDGE,"E5"),sQuery(id+"F6.wireOp",EDGE,"E6")])],"isStart":false});
            var sketch = newSketch(context, id + "F57", { "sketchPlane" : qUnion([Q0])});
            skLineSegment(sketch, "E97", {"start": v(-5.55, 51.72) * mm, "end": v(-5.55, -52.24) * mm});
            skLineSegment(sketch, "E98", {"start": v(0, 51.72) * mm, "end": v(0, -52.24) * mm});
            skLineSegment(sketch, "E99", {"start": v(5.03, 51.72) * mm, "end": v(5.03, -52.24) * mm});
            skSolve(sketch);
        }
        {
            var Q0;
            Q0=sQuery(id+"F57.wireOp",EDGE,"E97");
            var Q1;
            Q1=sQuery(id+"F57.wireOp",EDGE,"E98");
            var Q2;
            Q2=sQuery(id+"F57.wireOp",EDGE,"E99");
            extrude(context, id + "F58", {"bodyType" : ToolBodyType.SURFACE, "surfaceEntities" : qUnion([Q0, Q1, Q2]), "oppositeDirection" : true, "depth" : 1.27 * mm});
        }
        {
            var Q0;
            Q0=makeQuery(id+"F7.opExtrude","CAP_FACE",FACE,{"disambiguationData":[OSD([sQuery(id+"F0.wireOp",EDGE,"E0.bottom"),sQuery(id+"F0.wireOp",EDGE,"E0.top"),sQuery(id+"F6.wireOp",EDGE,"E5"),sQuery(id+"F6.wireOp",EDGE,"E6")])],"isStart":false});
            var sketch = newSketch(context, id + "F59", { "sketchPlane" : qUnion([Q0])});
            skLineSegment(sketch, "E100", {"start": v(-10.77, 44.15) * mm, "end": v(8.5, 44.15) * mm});
            skLineSegment(sketch, "E101", {"start": v(-10.77, 33.52) * mm, "end": v(8.5, 33.52) * mm});
            skLineSegment(sketch, "E102", {"start": v(-10.77, 23.6) * mm, "end": v(8.5, 23.6) * mm});
            skLineSegment(sketch, "E103", {"start": v(-10.77, 14.37) * mm, "end": v(8.5, 14.37) * mm});
            skLineSegment(sketch, "E104", {"start": v(-10.77, 2.19) * mm, "end": v(8.5, 2.19) * mm});
            skLineSegment(sketch, "E105", {"start": v(-10.77, -9.3) * mm, "end": v(8.5, -9.3) * mm});
            skLineSegment(sketch, "E106", {"start": v(-10.77, -19.93) * mm, "end": v(8.5, -19.93) * mm});
            skLineSegment(sketch, "E107", {"start": v(-10.77, -30.89) * mm, "end": v(8.5, -30.89) * mm});
            skLineSegment(sketch, "E108", {"start": v(-10.77, -43.88) * mm, "end": v(8.5, -43.88) * mm});
            skSolve(sketch);
        }
        {
            var Q0;
            Q0=sQuery(id+"F59.wireOp",EDGE,"E100");
            var Q1;
            Q1=sQuery(id+"F59.wireOp",EDGE,"E101");
            var Q2;
            Q2=sQuery(id+"F59.wireOp",EDGE,"E102");
            var Q3;
            Q3=sQuery(id+"F59.wireOp",EDGE,"E103");
            var Q4;
            Q4=sQuery(id+"F59.wireOp",EDGE,"E104");
            var Q5;
            Q5=sQuery(id+"F59.wireOp",EDGE,"E105");
            var Q6;
            Q6=sQuery(id+"F59.wireOp",EDGE,"E106");
            var Q7;
            Q7=sQuery(id+"F59.wireOp",EDGE,"E107");
            var Q8;
            Q8=sQuery(id+"F59.wireOp",EDGE,"E108");
            extrude(context, id + "F60", {"bodyType" : ToolBodyType.SURFACE, "surfaceEntities" : qUnion([Q0, Q1, Q2, Q3, Q4, Q5, Q6, Q7, Q8]), "oppositeDirection" : true, "depth" : 1.27 * mm});
        }
    });
